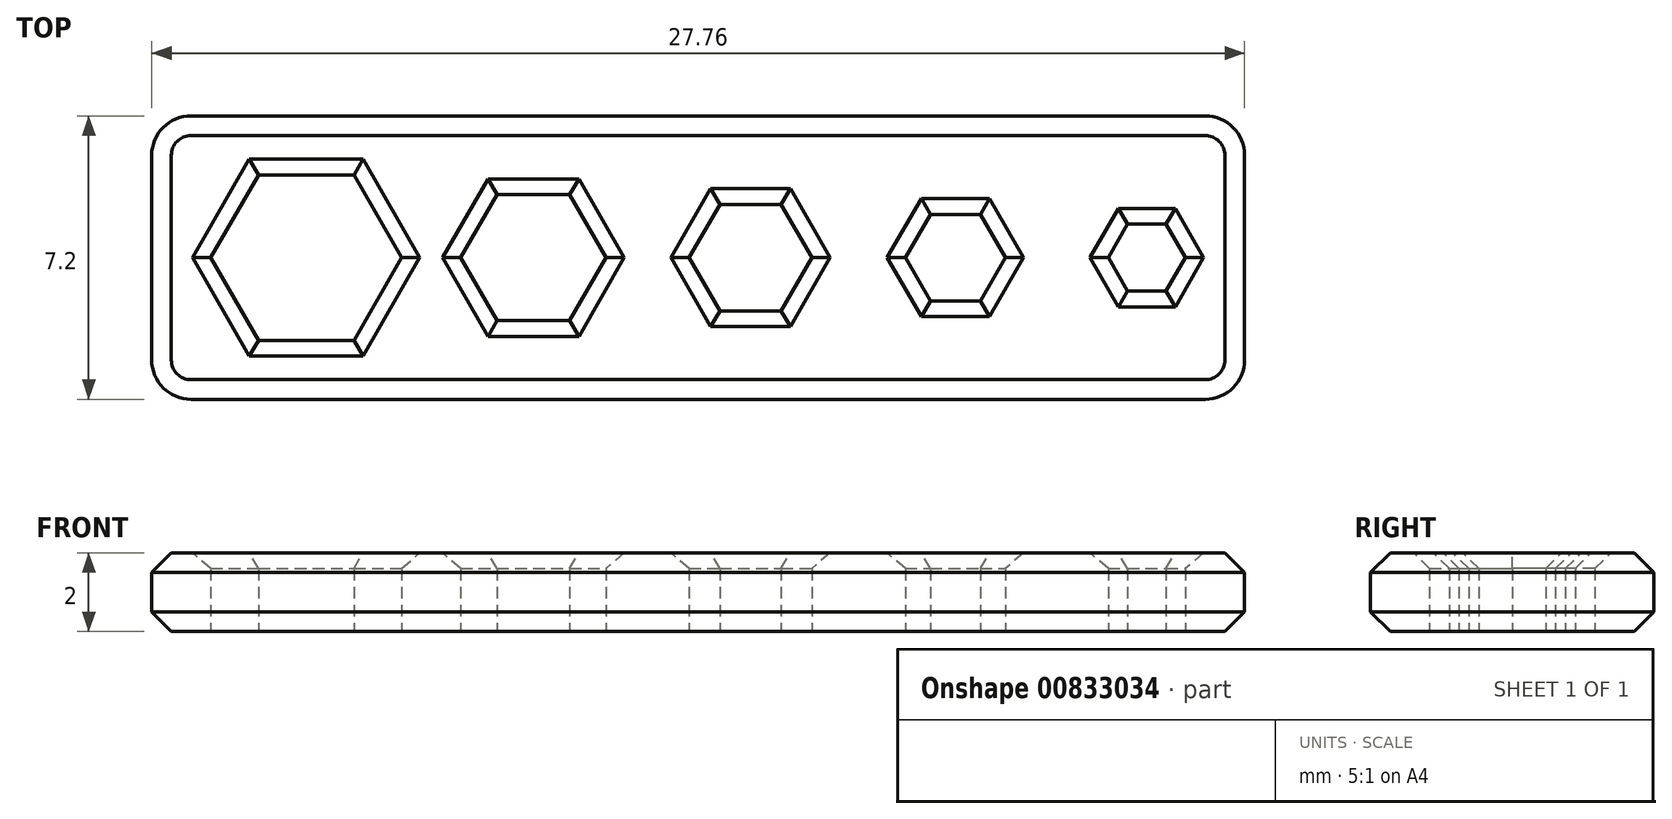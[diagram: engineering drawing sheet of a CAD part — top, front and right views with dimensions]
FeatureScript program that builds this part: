
annotation { "Feature Type Name" : "Feature", "Feature Type Description" : "" }
export const myFeature = defineFeature(function(context is Context, id is Id, definition is map)
    precondition{}
    {
        {
            var Q0;
            Q0=qCreatedBy(makeId("Top.planeOp"),FACE);
            var sketch = newSketch(context, id + "F0", { "sketchPlane" : qUnion([Q0])});
            skLineSegment(sketch, "E0", {"start": v(0, 0) * mm, "end": v(21.36, 0) * mm, "construction": true});
            skCircle(sketch, "E1.cCircle", {"center": v(0, 0) * mm, "radius": 2.1 * mm, "construction": true});
            skLineSegment(sketch, "E1.0", {"start": v(1.21, -2.1) * mm, "end": v(-1.21, -2.1) * mm});
            skLineSegment(sketch, "E1.1", {"start": v(-1.21, -2.1) * mm, "end": v(-2.42, 0) * mm});
            skLineSegment(sketch, "E1.2", {"start": v(-2.42, 0) * mm, "end": v(-1.21, 2.1) * mm});
            skLineSegment(sketch, "E1.3", {"start": v(-1.21, 2.1) * mm, "end": v(1.21, 2.1) * mm});
            skLineSegment(sketch, "E1.4", {"start": v(1.21, 2.1) * mm, "end": v(2.42, 0) * mm});
            skLineSegment(sketch, "E1.5", {"start": v(2.42, 0) * mm, "end": v(1.21, -2.1) * mm});
            skPoint(sketch, "E1.0.midPoint", {"position": v(0, -2.1) * mm});
            skCircle(sketch, "E2.cCircle", {"center": v(5.77, 0) * mm, "radius": 1.6 * mm, "construction": true});
            skLineSegment(sketch, "E2.0", {"start": v(6.7, -1.6) * mm, "end": v(4.85, -1.6) * mm});
            skLineSegment(sketch, "E2.1", {"start": v(4.85, -1.6) * mm, "end": v(3.92, 0) * mm});
            skLineSegment(sketch, "E2.2", {"start": v(3.92, 0) * mm, "end": v(4.85, 1.6) * mm});
            skLineSegment(sketch, "E2.3", {"start": v(4.85, 1.6) * mm, "end": v(6.7, 1.6) * mm});
            skLineSegment(sketch, "E2.4", {"start": v(6.7, 1.6) * mm, "end": v(7.62, 0) * mm});
            skLineSegment(sketch, "E2.5", {"start": v(7.62, 0) * mm, "end": v(6.7, -1.6) * mm});
            skPoint(sketch, "E2.0.midPoint", {"position": v(5.77, -1.6) * mm});
            skCircle(sketch, "E3.cCircle", {"center": v(11.29, 0) * mm, "radius": 1.35 * mm, "construction": true});
            skLineSegment(sketch, "E3.0", {"start": v(12.07, -1.35) * mm, "end": v(10.5, -1.35) * mm});
            skLineSegment(sketch, "E3.1", {"start": v(10.5, -1.35) * mm, "end": v(9.73, 0) * mm});
            skLineSegment(sketch, "E3.2", {"start": v(9.73, 0) * mm, "end": v(10.5, 1.35) * mm});
            skLineSegment(sketch, "E3.3", {"start": v(10.5, 1.35) * mm, "end": v(12.07, 1.35) * mm});
            skLineSegment(sketch, "E3.4", {"start": v(12.07, 1.35) * mm, "end": v(12.85, 0) * mm});
            skLineSegment(sketch, "E3.5", {"start": v(12.85, 0) * mm, "end": v(12.07, -1.35) * mm});
            skPoint(sketch, "E3.0.midPoint", {"position": v(11.29, -1.35) * mm});
            skCircle(sketch, "E4.cCircle", {"center": v(16.5, 0) * mm, "radius": 1.1 * mm, "construction": true});
            skLineSegment(sketch, "E4.0", {"start": v(17.13, -1.1) * mm, "end": v(15.86, -1.1) * mm});
            skLineSegment(sketch, "E4.1", {"start": v(15.86, -1.1) * mm, "end": v(15.22, 0) * mm});
            skLineSegment(sketch, "E4.2", {"start": v(15.22, 0) * mm, "end": v(15.86, 1.1) * mm});
            skLineSegment(sketch, "E4.3", {"start": v(15.86, 1.1) * mm, "end": v(17.13, 1.1) * mm});
            skLineSegment(sketch, "E4.4", {"start": v(17.13, 1.1) * mm, "end": v(17.76, 0) * mm});
            skLineSegment(sketch, "E4.5", {"start": v(17.76, 0) * mm, "end": v(17.13, -1.1) * mm});
            skPoint(sketch, "E4.0.midPoint", {"position": v(16.5, -1.1) * mm});
            skCircle(sketch, "E5.cCircle", {"center": v(21.36, 0) * mm, "radius": 0.85 * mm, "construction": true});
            skLineSegment(sketch, "E5.0", {"start": v(21.85, -0.85) * mm, "end": v(20.87, -0.85) * mm});
            skLineSegment(sketch, "E5.1", {"start": v(20.87, -0.85) * mm, "end": v(20.38, 0) * mm});
            skLineSegment(sketch, "E5.2", {"start": v(20.38, 0) * mm, "end": v(20.87, 0.85) * mm});
            skLineSegment(sketch, "E5.3", {"start": v(20.87, 0.85) * mm, "end": v(21.85, 0.85) * mm});
            skLineSegment(sketch, "E5.4", {"start": v(21.85, 0.85) * mm, "end": v(22.34, 0) * mm});
            skLineSegment(sketch, "E5.5", {"start": v(22.34, 0) * mm, "end": v(21.85, -0.85) * mm});
            skPoint(sketch, "E5.0.midPoint", {"position": v(21.36, -0.85) * mm});
            skLineSegment(sketch, "E6", {"start": v(1.21, -2.1) * mm, "end": v(3.92, 0) * mm, "construction": true});
            skLineSegment(sketch, "E7", {"start": v(6.7, -1.6) * mm, "end": v(9.73, 0) * mm, "construction": true});
            skLineSegment(sketch, "E8", {"start": v(12.07, -1.35) * mm, "end": v(15.22, 0) * mm, "construction": true});
            skLineSegment(sketch, "E9", {"start": v(17.13, -1.1) * mm, "end": v(20.38, 0) * mm, "construction": true});
            skLineSegment(sketch, "E10.bottom", {"start": v(-3.92, 3.6) * mm, "end": v(23.84, 3.6) * mm});
            skLineSegment(sketch, "E10.top", {"start": v(-3.92, -3.6) * mm, "end": v(23.84, -3.6) * mm});
            skLineSegment(sketch, "E10.left", {"start": v(-3.92, 3.6) * mm, "end": v(-3.92, -3.6) * mm});
            skLineSegment(sketch, "E10.right", {"start": v(23.84, 3.6) * mm, "end": v(23.84, -3.6) * mm});
            skLineSegment(sketch, "E11", {"start": v(-1.21, 2.1) * mm, "end": v(-1.21, 3.6) * mm, "construction": true});
            skLineSegment(sketch, "E12", {"start": v(-1.21, -2.1) * mm, "end": v(-1.21, -3.6) * mm, "construction": true});
            skLineSegment(sketch, "E13", {"start": v(-2.42, 0) * mm, "end": v(-3.92, 0) * mm, "construction": true});
            skLineSegment(sketch, "E14", {"start": v(22.34, 0) * mm, "end": v(23.84, 0) * mm, "construction": true});
            skSolve(sketch);
        }
        {
            var Q0;
            Q0=makeQuery(id+"F0.imprint","IMPRINT",FACE,{"disambiguationData":[TD([[makeQuery(id+"F0.imprint","IMPRINT",EDGE,{"derivedFrom":sQuery(id+"F0.wireOp",EDGE,"E1.0")}),1.0]])]});
            extrude(context, id + "F1", {"entities" : qUnion([Q0]), "depth" : 2 * mm, "offsetDistance" : 25 * mm});
        }
        {
            var Q0;
            Q0=makeQuery(id+"F1.opExtrude","SWEPT_EDGE",EDGE,{"disambiguationData":[OSD([sQuery(id+"F0.wireOp",EDGE,"E10.top"),sQuery(id+"F0.wireOp",EDGE,"E10.left")])]});
            var Q1;
            Q1=makeQuery(id+"F1.opExtrude","SWEPT_EDGE",EDGE,{"disambiguationData":[OSD([sQuery(id+"F0.wireOp",EDGE,"E10.top"),sQuery(id+"F0.wireOp",EDGE,"E10.right")])]});
            var Q2;
            Q2=makeQuery(id+"F1.opExtrude","SWEPT_EDGE",EDGE,{"disambiguationData":[OSD([sQuery(id+"F0.wireOp",EDGE,"E10.bottom"),sQuery(id+"F0.wireOp",EDGE,"E10.right")])]});
            var Q3;
            Q3=makeQuery(id+"F1.opExtrude","SWEPT_EDGE",EDGE,{"disambiguationData":[OSD([sQuery(id+"F0.wireOp",EDGE,"E10.bottom"),sQuery(id+"F0.wireOp",EDGE,"E10.left")])]});
            fillet(context, id + "F2", {"entities" : qUnion([Q0, Q1, Q2, Q3]), "radius" : 1 * mm, "tangentPropagation" : true, "allowEdgeOverflow" : false});
        }
        {
            var Q0;
            Q0=makeQuery(id+"F1.opExtrude","CAP_EDGE",EDGE,{"disambiguationData":[OSD([sQuery(id+"F0.wireOp",EDGE,"E10.top")])],"isStart":true});
            var Q1;
            Q1=makeQuery(id+"F1.opExtrude","CAP_EDGE",EDGE,{"disambiguationData":[OSD([sQuery(id+"F0.wireOp",EDGE,"E10.top")])],"isStart":false});
            chamfer(context, id + "F3", {"entities" : qUnion([Q0, Q1]), "width" : 0.5 * mm, "tangentPropagation" : true});
        }
        {
            var Q0;
            Q0=makeQuery(id+"F1.opExtrude","CAP_EDGE",EDGE,{"disambiguationData":[OSD([sQuery(id+"F0.wireOp",EDGE,"E1.1")])],"isStart":false});
            var Q1;
            Q1=makeQuery(id+"F1.opExtrude","CAP_EDGE",EDGE,{"disambiguationData":[OSD([sQuery(id+"F0.wireOp",EDGE,"E1.2")])],"isStart":false});
            var Q2;
            Q2=makeQuery(id+"F1.opExtrude","CAP_EDGE",EDGE,{"disambiguationData":[OSD([sQuery(id+"F0.wireOp",EDGE,"E1.3")])],"isStart":false});
            var Q3;
            Q3=makeQuery(id+"F1.opExtrude","CAP_EDGE",EDGE,{"disambiguationData":[OSD([sQuery(id+"F0.wireOp",EDGE,"E1.4")])],"isStart":false});
            var Q4;
            Q4=makeQuery(id+"F1.opExtrude","CAP_EDGE",EDGE,{"disambiguationData":[OSD([sQuery(id+"F0.wireOp",EDGE,"E1.5")])],"isStart":false});
            var Q5;
            Q5=makeQuery(id+"F1.opExtrude","CAP_EDGE",EDGE,{"disambiguationData":[OSD([sQuery(id+"F0.wireOp",EDGE,"E1.0")])],"isStart":false});
            var Q6;
            Q6=makeQuery(id+"F1.opExtrude","CAP_EDGE",EDGE,{"disambiguationData":[OSD([sQuery(id+"F0.wireOp",EDGE,"E2.1")])],"isStart":false});
            var Q7;
            Q7=makeQuery(id+"F1.opExtrude","CAP_EDGE",EDGE,{"disambiguationData":[OSD([sQuery(id+"F0.wireOp",EDGE,"E2.2")])],"isStart":false});
            var Q8;
            Q8=makeQuery(id+"F1.opExtrude","CAP_EDGE",EDGE,{"disambiguationData":[OSD([sQuery(id+"F0.wireOp",EDGE,"E2.3")])],"isStart":false});
            var Q9;
            Q9=makeQuery(id+"F1.opExtrude","CAP_EDGE",EDGE,{"disambiguationData":[OSD([sQuery(id+"F0.wireOp",EDGE,"E2.4")])],"isStart":false});
            var Q10;
            Q10=makeQuery(id+"F1.opExtrude","CAP_EDGE",EDGE,{"disambiguationData":[OSD([sQuery(id+"F0.wireOp",EDGE,"E2.5")])],"isStart":false});
            var Q11;
            Q11=makeQuery(id+"F1.opExtrude","CAP_EDGE",EDGE,{"disambiguationData":[OSD([sQuery(id+"F0.wireOp",EDGE,"E2.0")])],"isStart":false});
            var Q12;
            Q12=makeQuery(id+"F1.opExtrude","CAP_EDGE",EDGE,{"disambiguationData":[OSD([sQuery(id+"F0.wireOp",EDGE,"E3.0")])],"isStart":false});
            var Q13;
            Q13=makeQuery(id+"F1.opExtrude","CAP_EDGE",EDGE,{"disambiguationData":[OSD([sQuery(id+"F0.wireOp",EDGE,"E3.1")])],"isStart":false});
            var Q14;
            Q14=makeQuery(id+"F1.opExtrude","CAP_EDGE",EDGE,{"disambiguationData":[OSD([sQuery(id+"F0.wireOp",EDGE,"E3.2")])],"isStart":false});
            var Q15;
            Q15=makeQuery(id+"F1.opExtrude","CAP_EDGE",EDGE,{"disambiguationData":[OSD([sQuery(id+"F0.wireOp",EDGE,"E3.3")])],"isStart":false});
            var Q16;
            Q16=makeQuery(id+"F1.opExtrude","CAP_EDGE",EDGE,{"disambiguationData":[OSD([sQuery(id+"F0.wireOp",EDGE,"E3.4")])],"isStart":false});
            var Q17;
            Q17=makeQuery(id+"F1.opExtrude","CAP_EDGE",EDGE,{"disambiguationData":[OSD([sQuery(id+"F0.wireOp",EDGE,"E3.5")])],"isStart":false});
            var Q18;
            Q18=makeQuery(id+"F1.opExtrude","CAP_EDGE",EDGE,{"disambiguationData":[OSD([sQuery(id+"F0.wireOp",EDGE,"E4.1")])],"isStart":false});
            var Q19;
            Q19=makeQuery(id+"F1.opExtrude","CAP_EDGE",EDGE,{"disambiguationData":[OSD([sQuery(id+"F0.wireOp",EDGE,"E4.2")])],"isStart":false});
            var Q20;
            Q20=makeQuery(id+"F1.opExtrude","CAP_EDGE",EDGE,{"disambiguationData":[OSD([sQuery(id+"F0.wireOp",EDGE,"E4.3")])],"isStart":false});
            var Q21;
            Q21=makeQuery(id+"F1.opExtrude","CAP_EDGE",EDGE,{"disambiguationData":[OSD([sQuery(id+"F0.wireOp",EDGE,"E4.4")])],"isStart":false});
            var Q22;
            Q22=makeQuery(id+"F1.opExtrude","CAP_EDGE",EDGE,{"disambiguationData":[OSD([sQuery(id+"F0.wireOp",EDGE,"E4.5")])],"isStart":false});
            var Q23;
            Q23=makeQuery(id+"F1.opExtrude","CAP_EDGE",EDGE,{"disambiguationData":[OSD([sQuery(id+"F0.wireOp",EDGE,"E4.0")])],"isStart":false});
            var Q24;
            Q24=makeQuery(id+"F1.opExtrude","CAP_EDGE",EDGE,{"disambiguationData":[OSD([sQuery(id+"F0.wireOp",EDGE,"E5.0")])],"isStart":false});
            var Q25;
            Q25=makeQuery(id+"F1.opExtrude","CAP_EDGE",EDGE,{"disambiguationData":[OSD([sQuery(id+"F0.wireOp",EDGE,"E5.1")])],"isStart":false});
            var Q26;
            Q26=makeQuery(id+"F1.opExtrude","CAP_EDGE",EDGE,{"disambiguationData":[OSD([sQuery(id+"F0.wireOp",EDGE,"E5.2")])],"isStart":false});
            var Q27;
            Q27=makeQuery(id+"F1.opExtrude","CAP_EDGE",EDGE,{"disambiguationData":[OSD([sQuery(id+"F0.wireOp",EDGE,"E5.3")])],"isStart":false});
            var Q28;
            Q28=makeQuery(id+"F1.opExtrude","CAP_EDGE",EDGE,{"disambiguationData":[OSD([sQuery(id+"F0.wireOp",EDGE,"E5.4")])],"isStart":false});
            var Q29;
            Q29=makeQuery(id+"F1.opExtrude","CAP_EDGE",EDGE,{"disambiguationData":[OSD([sQuery(id+"F0.wireOp",EDGE,"E5.5")])],"isStart":false});
            chamfer(context, id + "F4", {"entities" : qUnion([Q0, Q1, Q2, Q3, Q4, Q5, Q6, Q7, Q8, Q9, Q10, Q11, Q12, Q13, Q14, Q15, Q16, Q17, Q18, Q19, Q20, Q21, Q22, Q23, Q24, Q25, Q26, Q27, Q28, Q29]), "width" : 0.4 * mm, "tangentPropagation" : true});
        }
    });
